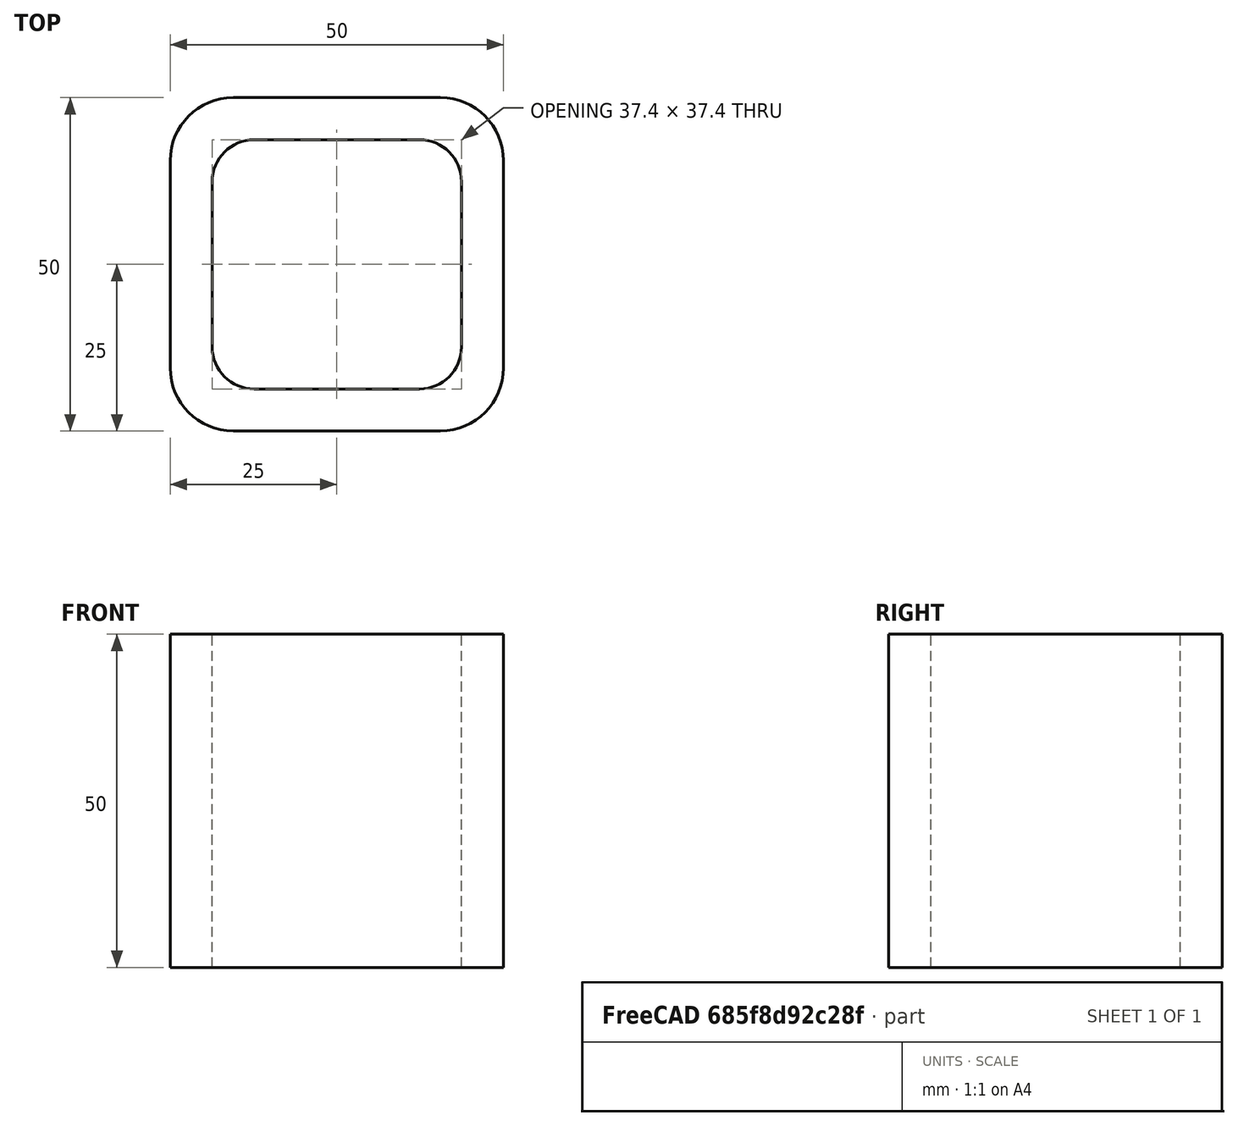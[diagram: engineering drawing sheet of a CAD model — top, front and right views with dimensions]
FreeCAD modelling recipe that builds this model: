
FCSTD DOCUMENT  (FreeCAD 0.15R4671 (Git))
Label: Square hollow section 50x50x6.3 EN10219 S235JRH
License: All rights reserved
LicenseURL: http://en.wikipedia.org/wiki/All_rights_reserved
objects: Sketcher::SketchObject×1, Part::Extrusion×1
note: 2 computed .brp shape members not serialized (recipe doc carries the construction recipe); baked Part::Feature solids carry a one-line shape summary decoded from their .brp

FEATURE [Sketcher::SketchObject] Sketch
  sketch-geometry (16):
    g0: LineSegment StartX=-12.4 StartY=18.7 StartZ=0 EndX=12.4 EndY=18.7 EndZ=0
    g1: LineSegment StartX=18.7 StartY=12.4 StartZ=0 EndX=18.7 EndY=-12.4 EndZ=0
    g2: LineSegment StartX=12.4 StartY=-18.7 StartZ=0 EndX=-12.4 EndY=-18.7 EndZ=0
    g3: LineSegment StartX=-18.7 StartY=-12.4 StartZ=0 EndX=-18.7 EndY=12.4 EndZ=0
    g4: LineSegment StartX=-15.55 StartY=25 StartZ=0 EndX=15.55 EndY=25 EndZ=0
    g5: LineSegment StartX=25 StartY=15.55 StartZ=0 EndX=25 EndY=-15.55 EndZ=0
    g6: LineSegment StartX=15.55 StartY=-25 StartZ=0 EndX=-15.55 EndY=-25 EndZ=0
    g7: LineSegment StartX=-25 StartY=-15.55 StartZ=0 EndX=-25 EndY=15.55 EndZ=0
    g8: ArcOfCircle CenterX=-12.4 CenterY=12.4 CenterZ=0 NormalX=0 NormalY=0 NormalZ=1 Radius=6.3 StartAngle=1.5708 EndAngle=3.14159
    g9: ArcOfCircle CenterX=12.4 CenterY=12.4 CenterZ=0 NormalX=0 NormalY=0 NormalZ=1 Radius=6.3 StartAngle=0 EndAngle=1.5708
    g10: ArcOfCircle CenterX=12.4 CenterY=-12.4 CenterZ=0 NormalX=0 NormalY=0 NormalZ=1 Radius=6.3 StartAngle=4.71239 EndAngle=6.28319
    g11: ArcOfCircle CenterX=-12.4 CenterY=-12.4 CenterZ=0 NormalX=0 NormalY=0 NormalZ=1 Radius=6.3 StartAngle=3.14159 EndAngle=4.71239
    g12: ArcOfCircle CenterX=15.55 CenterY=15.55 CenterZ=0 NormalX=0 NormalY=0 NormalZ=1 Radius=9.45 StartAngle=0 EndAngle=1.5708
    g13: ArcOfCircle CenterX=15.55 CenterY=-15.55 CenterZ=0 NormalX=0 NormalY=0 NormalZ=1 Radius=9.45 StartAngle=4.71239 EndAngle=6.28319
    g14: ArcOfCircle CenterX=-15.55 CenterY=-15.55 CenterZ=0 NormalX=0 NormalY=0 NormalZ=1 Radius=9.45 StartAngle=3.14159 EndAngle=4.71239
    g15: ArcOfCircle CenterX=-15.55 CenterY=15.55 CenterZ=0 NormalX=0 NormalY=0 NormalZ=1 Radius=9.45 StartAngle=1.5708 EndAngle=3.14159
  constraints (36):
    c: Horizontal(g2)
    c: Vertical(g3)
    c: Horizontal(g6)
    c: Vertical(g7)
    c: Tangent(g3,g8) = 1.5708
    c: Tangent(g0,g8) = 1.5708
    c: Tangent(g0,g9) = 1.5708
    c: Tangent(g1,g9) = 1.5708
    c: Tangent(g1,g10) = 1.5708
    c: Tangent(g2,g10) = 1.5708
    c: Tangent(g2,g11) = 1.5708
    c: Tangent(g3,g11) = 1.5708
    c: Tangent(g4,g12) = 1.5708
    c: Tangent(g5,g12) = 1.5708
    c: Tangent(g5,g13) = 1.5708
    c: Tangent(g6,g13) = 1.5708
    c: Tangent(g6,g14) = 1.5708
    c: Tangent(g7,g14) = 1.5708
    c: Tangent(g7,g15) = 1.5708
    c: Tangent(g4,g15) = 1.5708
    c: Equal(g9,g8)
    c: Equal(g9,g11)
    c: Equal(g9,g10)
    c: Equal(g12,g15)
    c: Equal(g12,g14)
    c: Equal(g12,g13)
    c: Symmetric(g4,g6,g-1)
    c: Symmetric(g7,g5,g-2)
    c: DistanceY(g4,g6) = -50
    c: DistanceX(g7,g5) = 50
    c: Symmetric(g3,g1,g-2)
    c: Symmetric(g0,g2,g-1)
    c: DistanceY(g0,g4) = 6.3
    c: DistanceX(g5,g1) = -6.3
    c: Radius(g9) = 6.3
    c: Radius(g12) = 9.45
FEATURE [Part::Extrusion] Extrude  label="Square hollow section 50x50x6.3 EN10219 S235JRH"
  Base = -> Sketch
  Dir = (0,0,50)
  Solid = true
